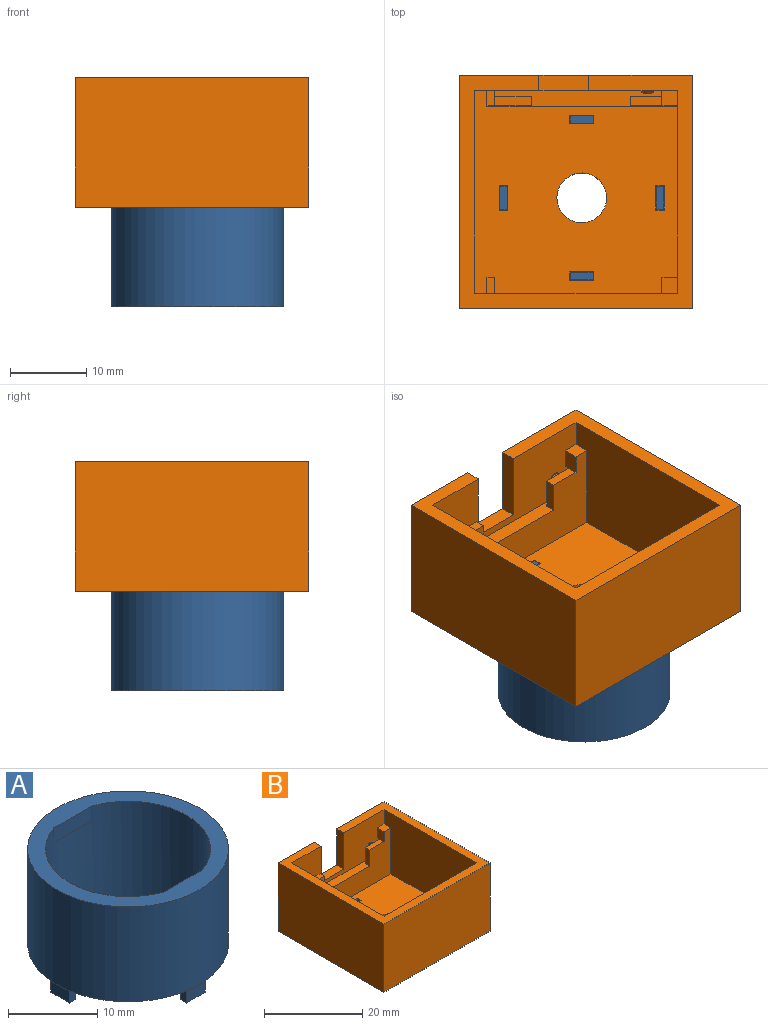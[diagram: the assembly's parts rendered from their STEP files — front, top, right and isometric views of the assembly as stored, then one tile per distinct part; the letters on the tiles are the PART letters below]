
ASSEMBLY  parts=2 mates=1
PART A: 28 faces, bbox 22.5x22.5x15 mm
  f0: cylinder r=9.25mm len=18.5mm, axis (0,0,-1), area 731.1mm2, adj f2,f3,f4,f5,f6,f7
  f1: cylinder r=11.25mm len=22.5mm, axis (0,0,-1), area 918.9mm2, adj f2,f3
  f2: plane 22.5x22.5mm, normal (0,0,1), area 132.8mm2, adj f0,f1,f5,f7
  f3: plane 22.5x22.5mm, normal (0,0,-1), area 116.8mm2, adj f0,f1,f8,f9,f10,f11,f13,f14
  f4: plane 6x0.5mm, normal (0,0,-1), area 2mm2, adj f0,f5
  f5: plane 6x2mm, normal (0,-1,0), area 12mm2, adj f0,f2,f4
  f6: plane 6x0.5mm, normal (0,0,-1), area 2mm2, adj f0,f7
  f7: plane 6x2mm, normal (0,1,0), area 12mm2, adj f0,f2,f6
  f8: plane 2x1mm, normal (0,-1,0), area 2mm2, adj f3,f9,f11,f12
  f9: plane 3x2mm, normal (-1,0,0), area 6mm2, adj f3,f8,f10,f12
  f10: plane 2x1mm, normal (0,1,0), area 2mm2, adj f3,f9,f11,f12
  f11: plane 3x2mm, normal (1,0,0), area 6mm2, adj f3,f8,f10,f12
  f12: plane 3x1mm, normal (0,0,-1), area 3mm2, adj f8,f9,f10,f11
  f13: plane 2x1mm, normal (-1,0,0), area 2mm2, adj f3,f14,f16,f17
  f14: plane 3x2mm, normal (0,1,0), area 6mm2, adj f3,f13,f15,f17
  f15: plane 2x1mm, normal (1,0,0), area 2mm2, adj f3,f14,f16,f17
  f16: plane 3x2mm, normal (0,-1,0), area 6mm2, adj f3,f13,f15,f17
  f17: plane 3x1mm, normal (0,0,-1), area 3mm2, adj f13,f14,f15,f16
  f18: plane 2x1mm, normal (0,-1,0), area 2mm2, adj f3,f19,f21,f22
  f19: plane 3x2mm, normal (-1,0,0), area 6mm2, adj f3,f18,f20,f22
  f20: plane 2x1mm, normal (0,1,0), area 2mm2, adj f3,f19,f21,f22
  f21: plane 3x2mm, normal (1,0,0), area 6mm2, adj f3,f18,f20,f22
  f22: plane 3x1mm, normal (0,0,-1), area 3mm2, adj f18,f19,f20,f21
  f23: plane 3x2mm, normal (0,-1,0), area 6mm2, adj f3,f24,f26,f27
  f24: plane 2x1mm, normal (-1,0,0), area 2mm2, adj f3,f23,f25,f27
  f25: plane 3x2mm, normal (0,1,0), area 6mm2, adj f3,f24,f26,f27
  f26: plane 2x1mm, normal (1,0,0), area 2mm2, adj f3,f23,f25,f27
  f27: plane 3x1mm, normal (0,0,-1), area 3mm2, adj f23,f24,f25,f26
PART B: 61 faces, bbox 30.5x30.5x17 mm
  f0: plane 27.9x26.5mm, normal (0,0,1), area 606.6mm2, adj f7,f8,f9,f11,f12,f15,f17,f18
  f1: plane 30.5x30.5mm, normal (0,0,-1), area 883mm2, adj f6,f13,f14,f16,f17,f45,f46,f47
  f2: plane 4.1x1.3mm, normal (0,0,1), area 5.3mm2, adj f4,f19,f34,f35
  f3: plane 2.5x2mm, normal (1,0,0), area 5mm2, adj f12,f19,f20,f32,f33
  f4: plane 2.5x2mm, normal (-1,0,0), area 5mm2, adj f2,f12,f19,f22,f41
  f5: plane 30.5x30.5mm, normal (0,0,1), area 215mm2, adj f6,f7,f11,f12,f13,f14,f15,f16
  f6: plane 30.5x17mm, normal (0,1,0), area 460mm2, adj f1,f5,f13,f16,f29,f30,f31
  f7: plane 26.5x15mm, normal (0,1,0), area 274.4mm2, adj f0,f5,f8,f10,f11,f15,f21,f24
  f8: plane 11.5x1.98mm, normal (1,0,0), area 22.8mm2, adj f0,f7,f10,f26
  f9: plane 11.5x0.99mm, normal (0,1,0), area 11.4mm2, adj f0,f10,f21,f26
  f10: plane 2x1mm, normal (0,0,1), area 2mm2, adj f7,f8,f9,f21,f26
  f11: plane 26.5x15mm, normal (-1,0,0), area 351.5mm2, adj f0,f5,f7,f12,f19,f22,f23,f25
  f12: plane 26.5x15mm, normal (0,-1,0), area 197.5mm2, adj f0,f3,f4,f5,f11,f15,f18,f20
  f13: plane 30.5x17mm, normal (-1,0,0), area 518.5mm2, adj f1,f5,f6,f14
  f14: plane 30.5x17mm, normal (0,-1,0), area 518.5mm2, adj f1,f5,f13,f16
  f15: plane 26.5x15mm, normal (1,0,0), area 397.5mm2, adj f0,f5,f7,f12
  f16: plane 30.5x17mm, normal (1,0,0), area 518.5mm2, adj f1,f5,f6,f14
  f17: cylinder r=3.25mm len=6.5mm, axis (0,0,-1), area 40.8mm2, adj f0,f1
  f18: plane 11.5x2mm, normal (-1,0,0), area 23mm2, adj f0,f12,f19,f20
  f19: plane 24.9x11.5mm, normal (0,-1,0), area 179.6mm2, adj f0,f2,f3,f4,f11,f18,f20,f22
  f20: plane 2x1mm, normal (0,0,1), area 2mm2, adj f3,f12,f18,f19
  f21: plane 11.5x2mm, normal (-1,0,0), area 23mm2, adj f0,f7,f9,f10
  f22: plane 2x2mm, normal (0,0,1), area 4mm2, adj f4,f11,f12,f19
  f23: plane 11.5x2mm, normal (0,1,0), area 23mm2, adj f0,f11,f24,f25
  f24: plane 11.5x2mm, normal (-1,0,0), area 23mm2, adj f0,f7,f23,f25
  f25: plane 2x2mm, normal (0,0,1), area 4mm2, adj f7,f11,f23,f24
  f26: cylinder r=6mm len=11.5mm, axis (0,0,-1), area 0.2mm2, adj f0,f8,f9,f10
  f27: cylinder r=6mm len=11.5mm, axis (0,0,-1), area 96.2mm2, adj f0,f7,f28
  f28: plane 7.7x1.4mm, normal (0,0,-1), area 7.4mm2, adj f7,f27
  f29: plane 9x2mm, normal (1,0,0), area 18mm2, adj f5,f6,f12,f31
  f30: plane 9x2mm, normal (-1,0,0), area 18mm2, adj f5,f6,f12,f31
  f31: plane 6.5x2mm, normal (0,0,1), area 13mm2, adj f6,f12,f29,f30
  f32: plane 4.8x1.3mm, normal (0,0,1), area 6.2mm2, adj f3,f19,f38,f39
  f33: plane 0.7x0.7mm, normal (0,0,-1), area 0.5mm2, adj f3,f12,f37,f38
  f34: plane 4x1.3mm, normal (-1,0,0), area 5.2mm2, adj f2,f19,f35,f40
  f35: plane 4.5x4mm, normal (0,1,0), area 18mm2, adj f2,f34,f36,f40,f41
  f36: plane 4x0.7mm, normal (-1,0,0), area 2.8mm2, adj f12,f35,f40,f41
  f37: plane 4x0.7mm, normal (1,0,0), area 2.8mm2, adj f12,f33,f38,f40
  f38: plane 5.5x4mm, normal (0,1,0), area 22mm2, adj f32,f33,f37,f39,f40
  f39: plane 4x1.3mm, normal (1,0,0), area 5.2mm2, adj f19,f32,f38,f40
  f40: plane 23x2mm, normal (0,0,1), area 33mm2, adj f12,f19,f34,f35,f36,f37,f38,f39
  f41: plane 0.7x0.4mm, normal (0,0,-1), area 0.3mm2, adj f4,f12,f35,f36
  f42: cylinder r=0.78mm len=1.56mm, axis (0,1,0), area 0.5mm2, adj f12,f44
  f43: plane 1.16x1.16mm, normal (0,-1,0), area 1.1mm2, adj f44
  f44: torus R=0.58mm, axis (0,-1,0), area 1.4mm2, adj f42,f43
  f45: plane 3.2x2mm, normal (-1,0,0), area 6.4mm2, adj f0,f1,f46,f48
  f46: plane 2x1.1mm, normal (0,1,0), area 2.2mm2, adj f0,f1,f45,f47
  f47: plane 3.2x2mm, normal (1,0,0), area 6.4mm2, adj f0,f1,f46,f48
  f48: plane 2x1.1mm, normal (0,-1,0), area 2.2mm2, adj f0,f1,f45,f47
  f49: plane 3.2x2mm, normal (0,-1,0), area 6.4mm2, adj f0,f1,f50,f52
  f50: plane 2x1.1mm, normal (-1,0,0), area 2.2mm2, adj f0,f1,f49,f51
  f51: plane 3.2x2mm, normal (0,1,0), area 6.4mm2, adj f0,f1,f50,f52
  f52: plane 2x1.1mm, normal (1,0,0), area 2.2mm2, adj f0,f1,f49,f51
  f53: plane 3.2x2mm, normal (1,0,0), area 6.4mm2, adj f0,f1,f54,f56
  f54: plane 2x1.1mm, normal (0,-1,0), area 2.2mm2, adj f0,f1,f53,f55
  f55: plane 3.2x2mm, normal (-1,0,0), area 6.4mm2, adj f0,f1,f54,f56
  f56: plane 2x1.1mm, normal (0,1,0), area 2.2mm2, adj f0,f1,f53,f55
  f57: plane 3.2x2mm, normal (0,1,0), area 6.4mm2, adj f0,f1,f58,f60
  f58: plane 2x1.1mm, normal (1,0,0), area 2.2mm2, adj f0,f1,f57,f59
  f59: plane 3.2x2mm, normal (0,-1,0), area 6.4mm2, adj f0,f1,f58,f60
  f60: plane 2x1.1mm, normal (-1,0,0), area 2.2mm2, adj f0,f1,f57,f59
PLACE A rot(axis=(-1,0,0),180deg) t=(-5.75,-14.39,-6.41)mm
PLACE B t=(-19.75,-0.39,-4.41)mm
MATE fastened B.f17 <-> A.f0  axis (0,0,-1) through (-5.75,-14.39,-6.41)mm
